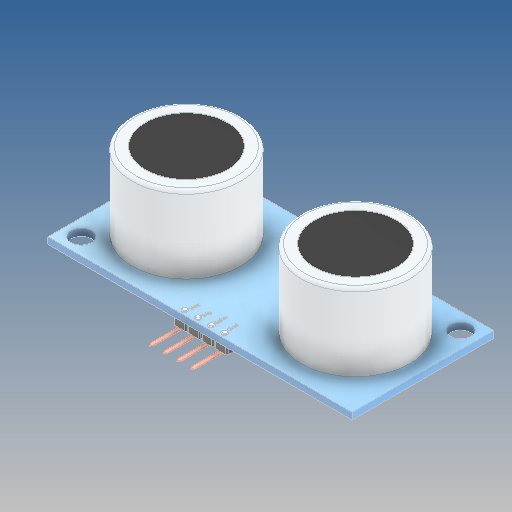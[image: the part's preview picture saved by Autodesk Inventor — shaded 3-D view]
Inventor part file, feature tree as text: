
AUTODESK INVENTOR PART (.ipt)
format: ipt  version: 2020 (Build 240168000, 168)  size: 765,952 bytes
history: mixed  units: mm
features: other x12, fillet x7, revolve x1, imported_body x1
ambient origin geometry x8: Origin, YZ Plane, XZ Plane, XY Plane, X Axis, Y Axis, Z Axis, Center Point
bodies: Solid1 (imported_parasolid), Solid2 (imported_parasolid), Solid3 (imported_parasolid), Solid4 (imported_parasolid), Solid5 (imported_parasolid), Solid6 (imported_parasolid), Solid7 (imported_parasolid), Solid8 (imported_parasolid), Solid9 (imported_parasolid), Solid10 (imported_parasolid), Solid11 (imported_parasolid), Solid12 (imported_parasolid), Solid13 (imported_parasolid), Solid14 (imported_parasolid), Solid15 (imported_parasolid), Solid16 (imported_parasolid), Solid17 (imported_parasolid), Solid18 (imported_parasolid), Solid19 (imported_parasolid), Solid20 (imported_parasolid)
feature tree (21):
  fillet  "Fillet1"  [1 undecoded]
  fillet  "Fillet2"  [1 undecoded]
  revolve  "Revolve1"  [1 undecoded]
  other  "LPattern2"
  other  "Boss-Extrude4[1]"
  other  "Boss-Extrude4[2]"
  other  "Boss-Extrude10[1]"
  other  "Boss-Extrude10[2]"
  other  "Boss-Extrude10[3]"
  other  "Boss-Extrude10[4]"
  fillet  "Fillet3"  [1 undecoded]
  fillet  "Fillet4"  [1 undecoded]
  fillet  "Fillet5"  [1 undecoded]
  fillet  "Fillet6"  [1 undecoded]
  other  "Cut-Extrude5"
  other  "Boss-Extrude11[1]"
  other  "Boss-Extrude11[2]"
  other  "Boss-Extrude11[3]"
  other  "Boss-Extrude11[4]"
  fillet  "Fillet7"  [1 undecoded]
  imported_body  NMx_Import_Brep_tag  [imported B-rep: ~124 faces, bbox_mm=[35.55, 13.54, 25.8]]
note: 8 required parameter values undecoded (feature->parameter linkage not recoverable at this tier; creation-order binding heuristic only, values carry confidence <= 0.55)
